# Revit family: 201_KCN-_
name_source: partatom
category: Air Terminals
units: mm (PartAtom-declared; Revit-internal decimal feet)

## family parameters
Always vertical = Yes
Cut with Voids When Loaded = No
Part Type = Normal
Room Calculation Point = Yes
Round Connector Dimension = Use Diameter
Shared = No
Work Plane-Based = No

## types (5) — shared parameters
CAT0 = Yes
CL_Location_5000 = 5000 mm  [stored 16.4042 ft]
Description = CHROME NICKEL–PLATED IN-OFF AIR VALVE
FL = 10 mm  [stored 0.0328084 ft]
L_ARR = 400 mm  [stored 1.31234 ft]
Manufacturer = Alnor
QmdConnectorList = 201;D
URL = http://www.ventilation-alnor.co.uk
W_ARR = 400 mm  [stored 1.31234 ft]
XRefLineVPlnId = 7453
YRefLineVPlnId = 7456
magiPartTypeId = 201
magiProductFamilyId = KCN-*
zero-valued in all types: CLBTZ, H_ARR

## per-type parameters (varying)
| type | D | DO | DO1 | magiProductId |
| KCN 100 | 100 mm | 168 mm  [stored 0.551181 ft] | 134 mm | KCN-100 |
| KCN 200 | 200 mm | 258 mm | 206 mm | KCN-200 |
| KCN 160 | 160 mm | 222 mm | 178 mm | KCN-160 |
| KCN 150 | 150 mm | 212 mm | 170 mm | KCN-150 |
| KCN 125 | 125 mm | 191 mm | 153 mm | KCN-125 |

note: column(s) folded — value = type name in every type: MC Product Code

note: [stored X ft] marks values corroborated as IEEE doubles in the binary element streams (Revit-internal decimal feet)

## geometry (parser evidence)
native form markers: Blend x2, Sweep x3
no freeform markers — native parametric forms only
